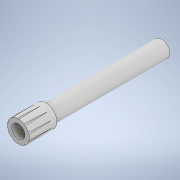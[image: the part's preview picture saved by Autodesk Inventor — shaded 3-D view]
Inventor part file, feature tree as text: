
AUTODESK INVENTOR PART (.ipt)
format: ipt  version: 2021 (Build 250183000, 183)  size: 165,376 bytes
history: native  units: in
note: dims shown in document units (in); Inventor stores cm internally (conversion verified against a paired STEP export)
features: sketch x5, plane x2, loft x2, revolve x1, pattern_circular x1
ambient origin geometry x8: Origin, YZ Plane, XZ Plane, XY Plane, X Axis, Y Axis, Z Axis, Center Point
bodies: Body1 (feature_tree)
feature tree (11):
  sketch  "Sketch1"  dims[d20=1.9685in d21=1.5748in]
  revolve  "Revolution2"  [1 undecoded]
  sketch  "Sketch6"  dims[d24=8.2677in d25=8.2677in d26=1.1811in]
  plane  "Work Plane1"
  loft  "Loft1"
  pattern_circular  "Circular Pattern2"  Count=3  [1 undecoded]
  sketch  "Sketch8"  dims[d29=-1.5748in]
  plane  "Work Plane2"
  loft  "Loft2"
  sketch  "Sketch7"  dims[d27=90.0deg d28=0.1181in]
  sketch  "Sketch9"  dims[d30=0.0039in d31=0.0in d32=90.0deg d33=0.0in d34=90.0deg d38=3.937in d39=360.0deg d41=0.9449in d42=-1.1811in d43=0.7874in d44=0.0in d45=90.0deg d46=0.0in d47=90.0deg d7=0.0197in d8=0.0344in d9=0.0197in d10=0.0344in]
note: 2 required parameter values undecoded (feature->parameter linkage not recoverable at this tier; creation-order binding heuristic only, values carry confidence <= 0.55)